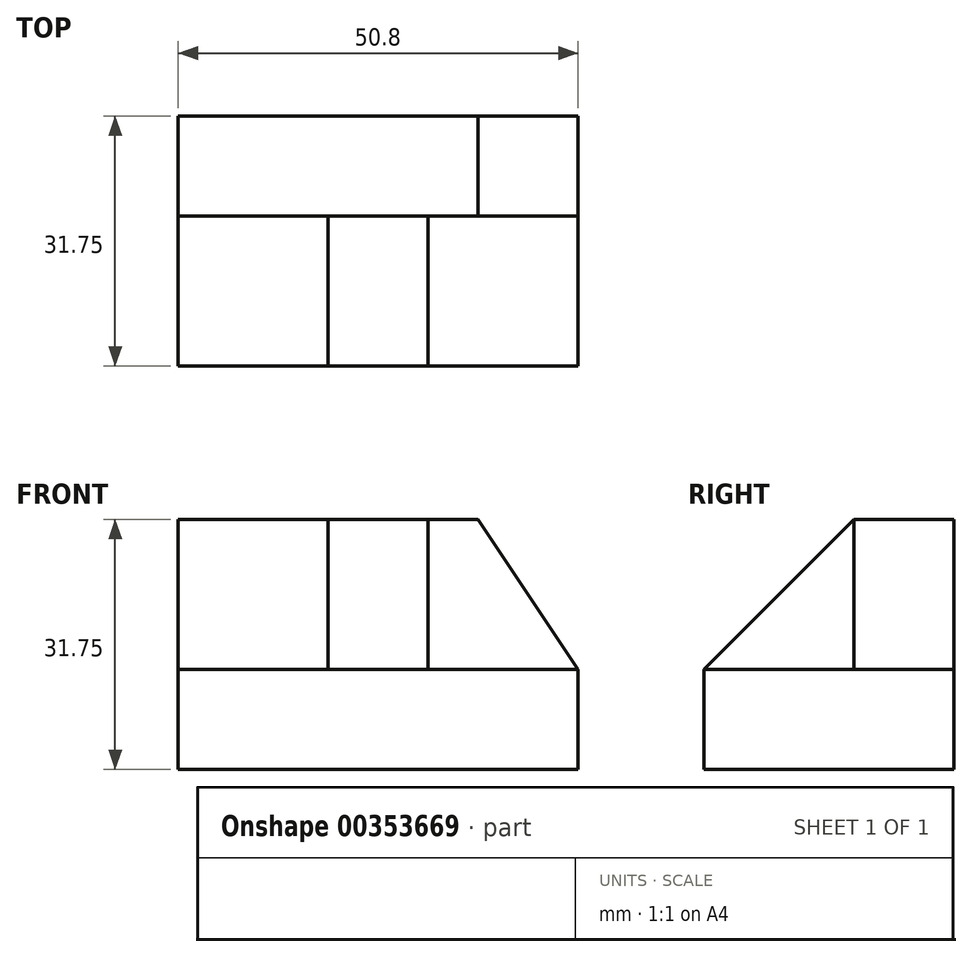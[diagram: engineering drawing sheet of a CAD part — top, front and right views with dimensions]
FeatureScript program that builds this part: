
annotation { "Feature Type Name" : "Feature", "Feature Type Description" : "" }
export const myFeature = defineFeature(function(context is Context, id is Id, definition is map)
    precondition{}
    {
        {
            var Q0;
            Q0=qCreatedBy(makeId("Front.planeOp"),FACE);
            var sketch = newSketch(context, id + "F0", { "sketchPlane" : qUnion([Q0])});
            skLineSegment(sketch, "E0", {"start": v(-50.8, 31.75) * mm, "end": v(-50.8, 0) * mm});
            skLineSegment(sketch, "E1", {"start": v(-50.8, 0) * mm, "end": v(0, 0) * mm});
            skLineSegment(sketch, "E2", {"start": v(0, 0) * mm, "end": v(0, 31.75) * mm});
            skLineSegment(sketch, "E3", {"start": v(0, 31.75) * mm, "end": v(-50.8, 31.75) * mm});
            skSolve(sketch);
        }
        {
            var Q0;
            Q0=makeQuery(id+"F0.imprint","IMPRINT",FACE,{"disambiguationData":[TD([[makeQuery(id+"F0.imprint","IMPRINT",EDGE,{"derivedFrom":sQuery(id+"F0.wireOp",EDGE,"E0")}),1.0]])]});
            extrude(context, id + "F1", {"entities" : qUnion([Q0]), "depth" : 31.75 * mm});
        }
        {
            var Q0;
            Q0=makeQuery(id+"F1.opExtrude","CAP_FACE",FACE,{"disambiguationData":[OSD([sQuery(id+"F0.wireOp",EDGE,"E0"),sQuery(id+"F0.wireOp",EDGE,"E1"),sQuery(id+"F0.wireOp",EDGE,"E2"),sQuery(id+"F0.wireOp",EDGE,"E3")])],"isStart":false});
            var sketch = newSketch(context, id + "F2", { "sketchPlane" : qUnion([Q0])});
            skLineSegment(sketch, "E4", {"start": v(-31.75, 31.75) * mm, "end": v(-31.75, 12.7) * mm});
            skLineSegment(sketch, "E5", {"start": v(-31.75, 12.7) * mm, "end": v(-50.8, 12.7) * mm});
            skLineSegment(sketch, "E6", {"start": v(-19.05, 31.75) * mm, "end": v(-19.05, 12.7) * mm});
            skLineSegment(sketch, "E7", {"start": v(-19.05, 12.7) * mm, "end": v(0, 12.7) * mm});
            skSolve(sketch);
        }
        {
            var Q0;
            {var subQ0=sQuery(id+"F2.wireOp",EDGE,"E4");Q0=makeQuery(id+"F2.imprint","IMPRINT",FACE,{"disambiguationData":[TD([[makeQuery(id+"F2.imprint","IMPRINT",EDGE,{"derivedFrom":subQ0}),-1.0]])]});}
            var Q1;
            {var subQ0=sQuery(id+"F2.wireOp",EDGE,"E6");Q1=makeQuery(id+"F2.imprint","IMPRINT",FACE,{"disambiguationData":[TD([[makeQuery(id+"F2.imprint","IMPRINT",EDGE,{"derivedFrom":subQ0}),1.0]])]});}
            extrude(context, id + "F3", {"entities" : qUnion([Q0, Q1]), "operationType" : NewBodyOperationType.REMOVE, "oppositeDirection" : true, "depth" : 19.05 * mm});
        }
        {
            var Q0;
            Q0=makeQuery(id+"F3.boolean.opBoolean","COPY",FACE,{"derivedFrom":makeQuery(id+"F3.opExtrude","SWEPT_FACE",FACE,{"disambiguationData":[OSD([sQuery(id+"F2.wireOp",EDGE,"E6")])]})});
            var sketch = newSketch(context, id + "F4", { "sketchPlane" : qUnion([Q0])});
            skLineSegment(sketch, "E8", {"start": v(-12.7, 31.75) * mm, "end": v(-31.75, 12.7) * mm});
            skSolve(sketch);
        }
        {
            var Q0;
            Q0=makeQuery(id+"F4.imprint","IMPRINT",FACE,{"disambiguationData":[TD([[makeQuery(id+"F4.imprint","IMPRINT",EDGE,{"derivedFrom":sQuery(id+"F4.wireOp",EDGE,"E8")}),-1.0]])]});
            extrude(context, id + "F5", {"entities" : qUnion([Q0]), "operationType" : NewBodyOperationType.REMOVE, "oppositeDirection" : true, "depth" : 19.05 * mm});
        }
        {
            var Q0;
            Q0=makeQuery(id+"F3.boolean.opBoolean","COPY",FACE,{"derivedFrom":makeQuery(id+"F3.opExtrude","CAP_FACE",FACE,{"disambiguationData":[OSD([sQuery(id+"F0.wireOp",EDGE,"E2"),sQuery(id+"F0.wireOp",EDGE,"E3"),sQuery(id+"F2.wireOp",EDGE,"E6"),sQuery(id+"F2.wireOp",EDGE,"E7")])],"isStart":false})});
            var sketch = newSketch(context, id + "F6", { "sketchPlane" : qUnion([Q0])});
            skLineSegment(sketch, "E9", {"start": v(-12.7, 31.75) * mm, "end": v(0, 12.7) * mm});
            skSolve(sketch);
        }
        {
            var Q0;
            {var subQ0=sQuery(id+"F6.wireOp",EDGE,"E9");Q0=makeQuery(id+"F6.imprint","IMPRINT",FACE,{"disambiguationData":[TD([[makeQuery(id+"F6.imprint","IMPRINT",EDGE,{"derivedFrom":subQ0}),1.0]])]});}
            extrude(context, id + "F7", {"entities" : qUnion([Q0]), "operationType" : NewBodyOperationType.REMOVE, "oppositeDirection" : true, "depth" : 12.7 * mm});
        }
    });
